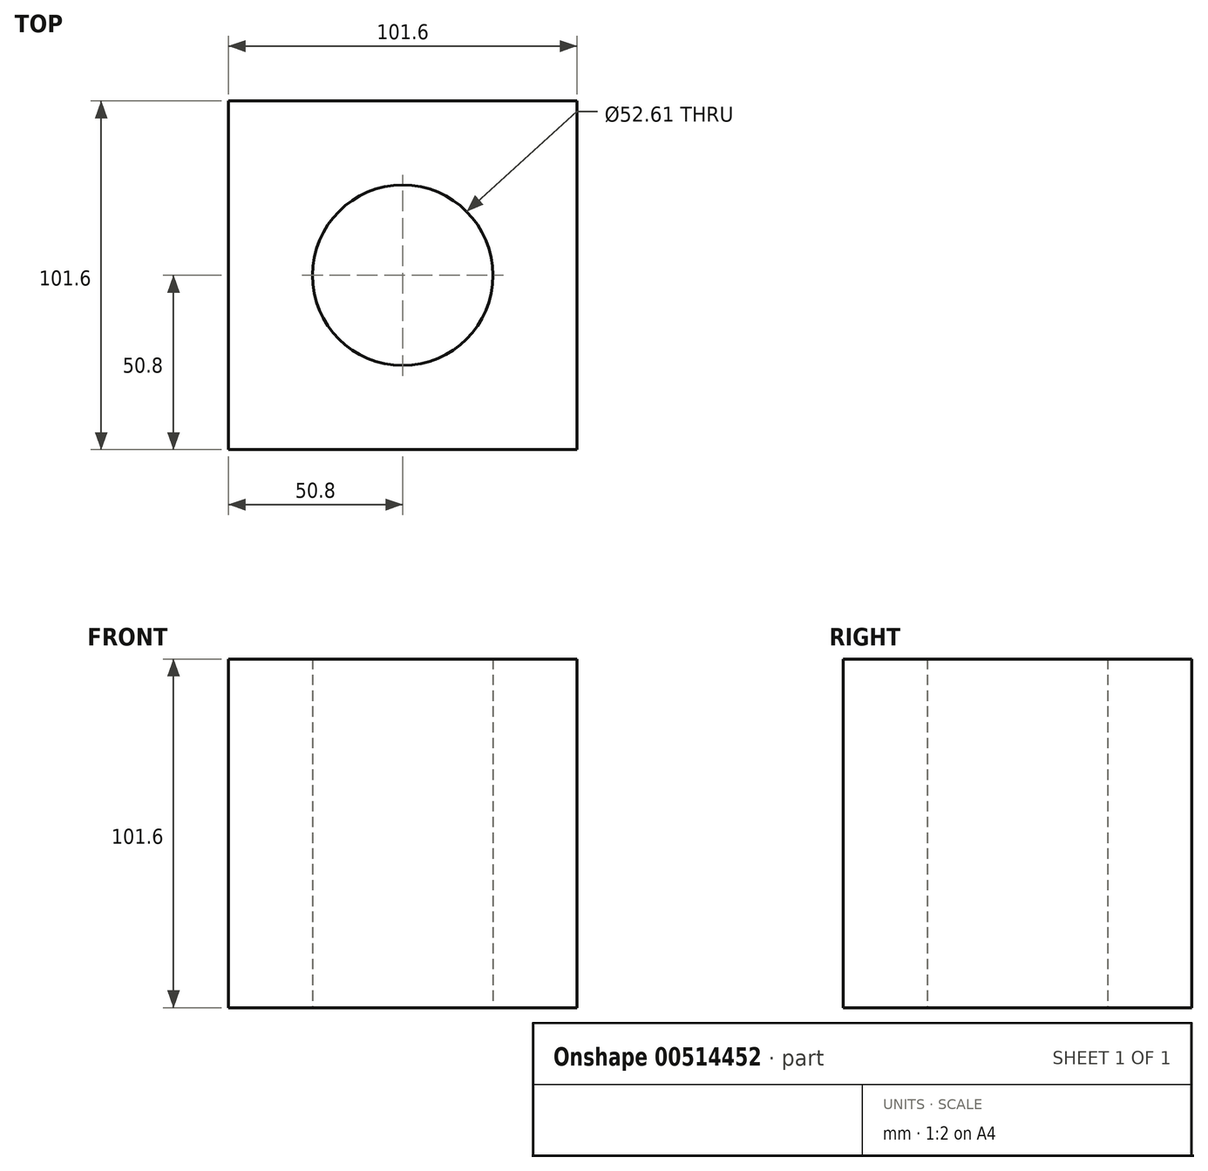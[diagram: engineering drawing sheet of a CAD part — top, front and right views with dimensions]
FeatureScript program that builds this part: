
annotation { "Feature Type Name" : "Feature", "Feature Type Description" : "" }
export const myFeature = defineFeature(function(context is Context, id is Id, definition is map)
    precondition{}
    {
        {
            var Q0;
            Q0=qCreatedBy(makeId("Top.planeOp"),FACE);
            var sketch = newSketch(context, id + "F0", { "sketchPlane" : qUnion([Q0])});
            skLineSegment(sketch, "E0.bottom", {"start": v(-50.8, 50.8) * mm, "end": v(50.8, 50.8) * mm});
            skLineSegment(sketch, "E0.top", {"start": v(-50.8, -50.8) * mm, "end": v(50.8, -50.8) * mm});
            skLineSegment(sketch, "E0.left", {"start": v(-50.8, 50.8) * mm, "end": v(-50.8, -50.8) * mm});
            skLineSegment(sketch, "E0.right", {"start": v(50.8, 50.8) * mm, "end": v(50.8, -50.8) * mm});
            skPoint(sketch, "E0.middle", {"position": v(0, 0) * mm});
            skCircle(sketch, "E1", {"center": v(0, 0) * mm, "radius": 26.3 * mm});
            skSolve(sketch);
        }
        {
            var Q0;
            Q0=makeQuery(id+"F0.imprint","IMPRINT",FACE,{"disambiguationData":[TD([[makeQuery(id+"F0.imprint","IMPRINT",EDGE,{"derivedFrom":sQuery(id+"F0.wireOp",EDGE,"E0.bottom")}),-1.0]])]});
            extrude(context, id + "F1", {"entities" : qUnion([Q0]), "depth" : 101.6 * mm});
        }
    });
